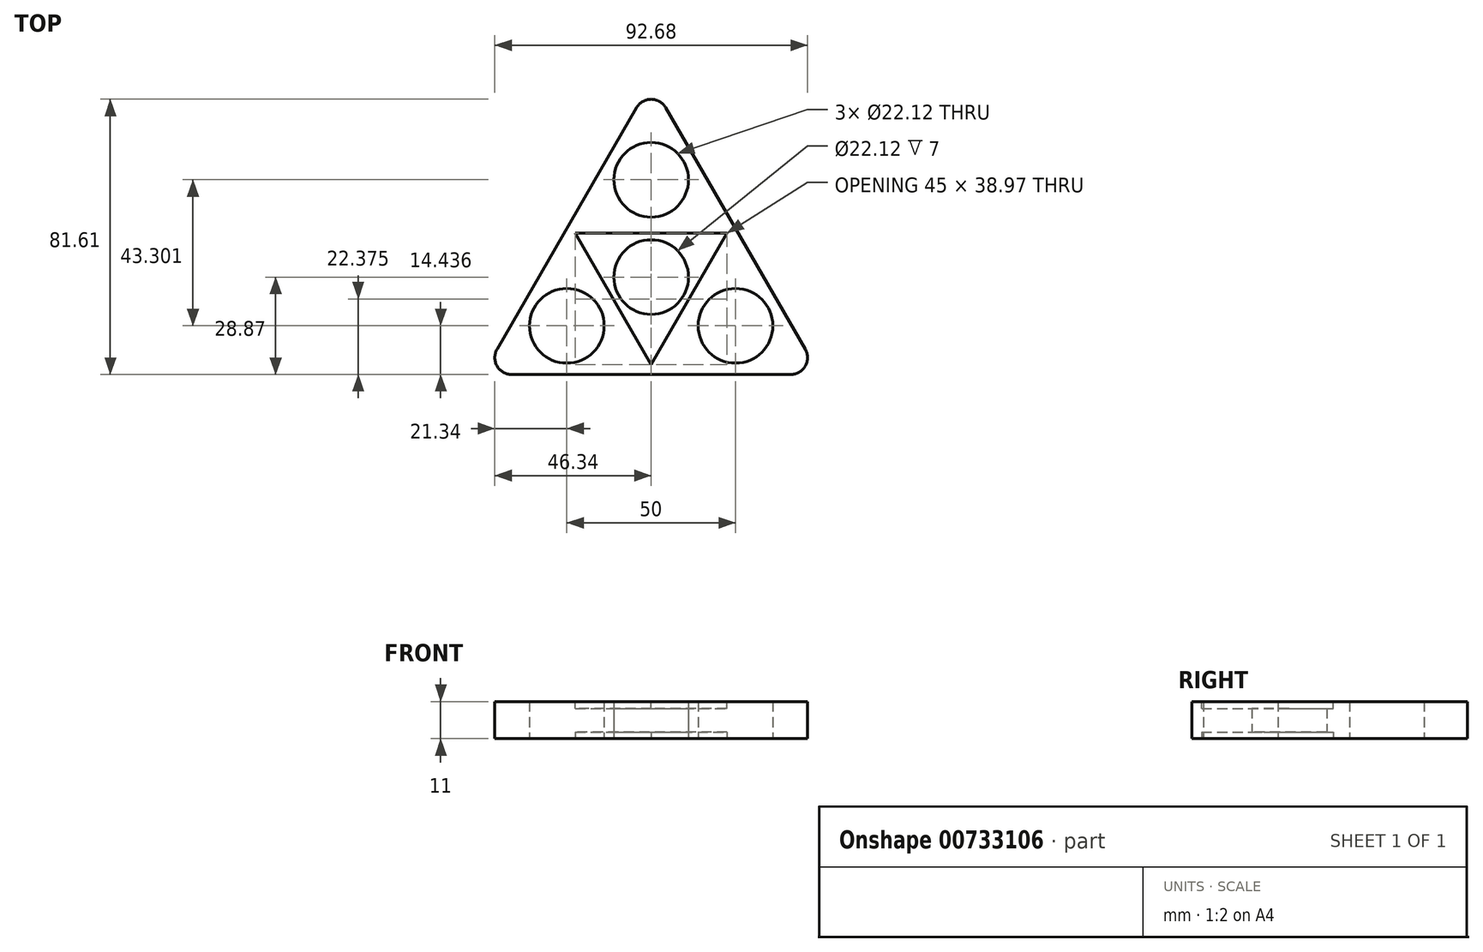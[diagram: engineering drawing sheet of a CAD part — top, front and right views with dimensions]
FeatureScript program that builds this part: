
annotation { "Feature Type Name" : "Feature", "Feature Type Description" : "" }
export const myFeature = defineFeature(function(context is Context, id is Id, definition is map)
    precondition{}
    {
        {
            var Q0;
            Q0=qCreatedBy(makeId("Top.planeOp"),FACE);
            var sketch = newSketch(context, id + "F0", { "sketchPlane" : qUnion([Q0])});
            skCircle(sketch, "E0", {"center": v(0, 28.87) * mm, "radius": 11.06 * mm});
            skCircle(sketch, "E1", {"center": v(0, 0) * mm, "radius": 11.06 * mm});
            skCircle(sketch, "E2", {"center": v(25, -14.43) * mm, "radius": 11.06 * mm});
            skCircle(sketch, "E3", {"center": v(-25, -14.43) * mm, "radius": 11.06 * mm});
            skLineSegment(sketch, "E4", {"start": v(0, 0) * mm, "end": v(0, 28.87) * mm, "construction": true});
            skLineSegment(sketch, "E5", {"start": v(25, -14.43) * mm, "end": v(0, 0) * mm, "construction": true});
            skLineSegment(sketch, "E6", {"start": v(-25, -14.43) * mm, "end": v(0, 0) * mm, "construction": true});
            skLineSegment(sketch, "E7", {"start": v(0, 28.87) * mm, "end": v(25, -14.43) * mm, "construction": true});
            skLineSegment(sketch, "E8", {"start": v(25, -14.43) * mm, "end": v(-25, -14.43) * mm, "construction": true});
            skLineSegment(sketch, "E9", {"start": v(0, 28.87) * mm, "end": v(-25, -14.43) * mm, "construction": true});
            skLineSegment(sketch, "E10", {"start": v(0, 57.74) * mm, "end": v(-25, 14.43) * mm});
            skLineSegment(sketch, "E11", {"start": v(-25, 14.43) * mm, "end": v(25, 14.43) * mm});
            skLineSegment(sketch, "E12", {"start": v(25, 14.43) * mm, "end": v(0, 57.74) * mm});
            skLineSegment(sketch, "E13", {"start": v(-25, 14.43) * mm, "end": v(-50, -28.87) * mm});
            skLineSegment(sketch, "E14", {"start": v(-50, -28.87) * mm, "end": v(0, -28.87) * mm});
            skLineSegment(sketch, "E15", {"start": v(0, -28.87) * mm, "end": v(-25, 14.43) * mm});
            skLineSegment(sketch, "E16", {"start": v(25, 14.43) * mm, "end": v(0, -28.87) * mm});
            skLineSegment(sketch, "E17", {"start": v(0, -28.87) * mm, "end": v(50, -28.87) * mm});
            skLineSegment(sketch, "E18", {"start": v(50, -28.87) * mm, "end": v(25, 14.43) * mm});
            skLineSegment(sketch, "E19", {"start": v(0, 57.74) * mm, "end": v(0, 0) * mm, "construction": true});
            skLineSegment(sketch, "E20", {"start": v(-50, -28.87) * mm, "end": v(0, 0) * mm, "construction": true});
            skLineSegment(sketch, "E21", {"start": v(50, -28.87) * mm, "end": v(0, 0) * mm, "construction": true});
            skSolve(sketch);
        }
        {
            var Q0;
            Q0=makeQuery(id+"F0.imprint","IMPRINT",FACE,{"disambiguationData":[TD([[makeQuery(id+"F0.imprint","IMPRINT",EDGE,{"derivedFrom":sQuery(id+"F0.wireOp",EDGE,"E0")}),-1.0]])]});
            var Q1;
            Q1=makeQuery(id+"F0.imprint","IMPRINT",FACE,{"disambiguationData":[TD([[makeQuery(id+"F0.imprint","IMPRINT",EDGE,{"derivedFrom":sQuery(id+"F0.wireOp",EDGE,"E3")}),-1.0]])]});
            var Q2;
            Q2=makeQuery(id+"F0.imprint","IMPRINT",FACE,{"disambiguationData":[TD([[makeQuery(id+"F0.imprint","IMPRINT",EDGE,{"derivedFrom":sQuery(id+"F0.wireOp",EDGE,"E2")}),-1.0]])]});
            var Q3;
            Q3=makeQuery(id+"F0.imprint","IMPRINT",FACE,{"disambiguationData":[TD([[makeQuery(id+"F0.imprint","IMPRINT",EDGE,{"derivedFrom":sQuery(id+"F0.wireOp",EDGE,"E1")}),-1.0]])]});
            extrude(context, id + "F1", {"entities" : qUnion([Q0, Q1, Q2, Q3]), "depth" : 11 * mm, "offsetDistance" : 25 * mm});
        }
        {
            var Q0;
            Q0=makeQuery(id+"F1.opExtrude","SWEPT_EDGE",EDGE,{"disambiguationData":[OSD([sQuery(id+"F0.wireOp",EDGE,"E17"),sQuery(id+"F0.wireOp",EDGE,"E18")])]});
            var Q1;
            Q1=makeQuery(id+"F1.opExtrude","SWEPT_EDGE",EDGE,{"disambiguationData":[OSD([sQuery(id+"F0.wireOp",EDGE,"E10"),sQuery(id+"F0.wireOp",EDGE,"E12")])]});
            var Q2;
            Q2=makeQuery(id+"F1.opExtrude","SWEPT_EDGE",EDGE,{"disambiguationData":[OSD([sQuery(id+"F0.wireOp",EDGE,"E13"),sQuery(id+"F0.wireOp",EDGE,"E14")])]});
            fillet(context, id + "F2", {"entities" : qUnion([Q0, Q1, Q2]), "radius" : 5 * mm, "tangentPropagation" : true, "allowEdgeOverflow" : false});
        }
        {
            var Q0;
            Q0=makeQuery(id+"F1.opExtrude","CAP_FACE",FACE,{"disambiguationData":[OSD([sQuery(id+"F0.wireOp",EDGE,"E0"),sQuery(id+"F0.wireOp",EDGE,"E1"),sQuery(id+"F0.wireOp",EDGE,"E2"),sQuery(id+"F0.wireOp",EDGE,"E3"),sQuery(id+"F0.wireOp",EDGE,"E10"),sQuery(id+"F0.wireOp",EDGE,"E12"),sQuery(id+"F0.wireOp",EDGE,"E13"),sQuery(id+"F0.wireOp",EDGE,"E14"),sQuery(id+"F0.wireOp",EDGE,"E17"),sQuery(id+"F0.wireOp",EDGE,"E18")])],"isStart":false});
            var sketch = newSketch(context, id + "F3", { "sketchPlane" : qUnion([Q0])});
            skLineSegment(sketch, "E22", {"start": v(0, -25.98) * mm, "end": v(-22.5, 13) * mm});
            skLineSegment(sketch, "E23", {"start": v(-22.5, 13) * mm, "end": v(22.5, 13) * mm});
            skLineSegment(sketch, "E24", {"start": v(22.5, 13) * mm, "end": v(0, -25.98) * mm});
            skLineSegment(sketch, "E25", {"start": v(0, 0) * mm, "end": v(22.5, 13) * mm, "construction": true});
            skLineSegment(sketch, "E26", {"start": v(0, 0) * mm, "end": v(-22.5, 13) * mm, "construction": true});
            skLineSegment(sketch, "E27", {"start": v(0, 0) * mm, "end": v(0, -25.98) * mm, "construction": true});
            skSolve(sketch);
        }
        {
            var Q0;
            Q0=makeQuery(id+"F3.imprint","IMPRINT",FACE,{"disambiguationData":[TD([[makeQuery(id+"F3.imprint","IMPRINT",EDGE,{"derivedFrom":sQuery(id+"F3.wireOp",EDGE,"E22")}),-1.0]])]});
            extrude(context, id + "F4", {"entities" : qUnion([Q0]), "operationType" : NewBodyOperationType.REMOVE, "oppositeDirection" : true, "depth" : 2 * mm, "offsetDistance" : 25 * mm});
        }
        {
            var Q0;
            Q0=makeQuery(id+"F1.opExtrude","CAP_FACE",FACE,{"disambiguationData":[OSD([sQuery(id+"F0.wireOp",EDGE,"E0"),sQuery(id+"F0.wireOp",EDGE,"E1"),sQuery(id+"F0.wireOp",EDGE,"E2"),sQuery(id+"F0.wireOp",EDGE,"E3"),sQuery(id+"F0.wireOp",EDGE,"E10"),sQuery(id+"F0.wireOp",EDGE,"E12"),sQuery(id+"F0.wireOp",EDGE,"E13"),sQuery(id+"F0.wireOp",EDGE,"E14"),sQuery(id+"F0.wireOp",EDGE,"E17"),sQuery(id+"F0.wireOp",EDGE,"E18")])],"isStart":true});
            var sketch = newSketch(context, id + "F5", { "sketchPlane" : qUnion([Q0])});
            skLineSegment(sketch, "E28", {"start": v(22.5, -13) * mm, "end": v(-22.5, -13) * mm});
            skLineSegment(sketch, "E29", {"start": v(-22.5, -13) * mm, "end": v(0, 25.98) * mm});
            skLineSegment(sketch, "E30", {"start": v(0, 25.98) * mm, "end": v(22.5, -13) * mm});
            skLineSegment(sketch, "E31", {"start": v(22.5, -13) * mm, "end": v(0, 0) * mm, "construction": true});
            skLineSegment(sketch, "E32", {"start": v(0, 0) * mm, "end": v(-22.5, -13) * mm, "construction": true});
            skLineSegment(sketch, "E33", {"start": v(0, 25.98) * mm, "end": v(0, 0) * mm, "construction": true});
            skSolve(sketch);
        }
        {
            var Q0;
            Q0 = qSketchRegion(id + "F5", true);
            extrude(context, id + "F6", {"entities" : qUnion([Q0]), "operationType" : NewBodyOperationType.REMOVE, "oppositeDirection" : true, "depth" : 2 * mm, "offsetDistance" : 25 * mm});
        }
    });
